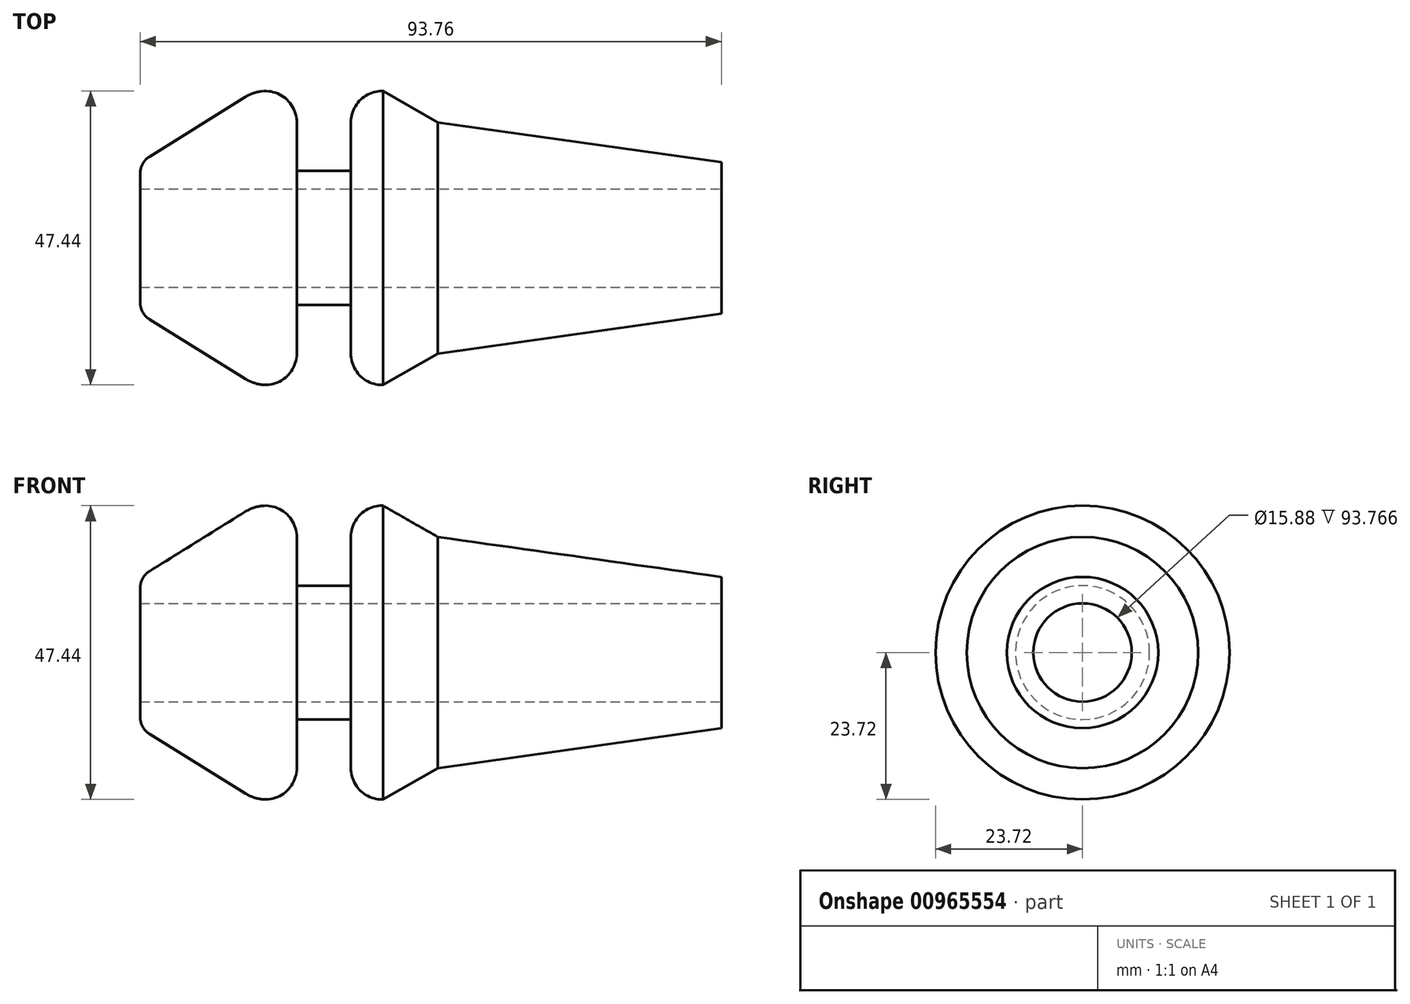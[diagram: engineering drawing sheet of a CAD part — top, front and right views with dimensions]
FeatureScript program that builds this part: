
annotation { "Feature Type Name" : "Feature", "Feature Type Description" : "" }
export const myFeature = defineFeature(function(context is Context, id is Id, definition is map)
    precondition{}
    {
        {
            var Q0;
            Q0=qCreatedBy(makeId("Top.planeOp"),FACE);
            var sketch = newSketch(context, id + "F0", { "sketchPlane" : qUnion([Q0])});
            skLineSegment(sketch, "E0", {"start": v(-39.16, 0) * mm, "end": v(-39.16, 12.21) * mm});
            skLineSegment(sketch, "E1", {"start": v(-39.16, 12.21) * mm, "end": v(-20.63, 23.72) * mm});
            skLineSegment(sketch, "E2", {"start": v(-20.63, 23.72) * mm, "end": v(-13.9, 23.72) * mm});
            skLineSegment(sketch, "E3", {"start": v(0, 23.72) * mm, "end": v(8.84, 18.67) * mm});
            skLineSegment(sketch, "E4", {"start": v(8.84, 18.67) * mm, "end": v(54.6, 12.21) * mm});
            skLineSegment(sketch, "E5", {"start": v(54.6, 12.21) * mm, "end": v(54.6, 0) * mm});
            skLineSegment(sketch, "E6", {"start": v(-39.16, 0) * mm, "end": v(54.6, 0) * mm});
            skLineSegment(sketch, "E7", {"start": v(-13.9, 23.72) * mm, "end": v(-13.9, 10.8) * mm});
            skLineSegment(sketch, "E8", {"start": v(-13.9, 10.8) * mm, "end": v(-5.2, 10.8) * mm});
            skLineSegment(sketch, "E9", {"start": v(-5.2, 10.8) * mm, "end": v(-5.2, 23.72) * mm});
            skLineSegment(sketch, "E10.trimOffspring", {"start": v(-5.2, 23.72) * mm, "end": v(0, 23.72) * mm});
            skSolve(sketch);
        }
        {
            var Q0;
            Q0=makeQuery(id+"F0.imprint","IMPRINT",FACE,{"disambiguationData":[TD([[makeQuery(id+"F0.imprint","IMPRINT",EDGE,{"derivedFrom":sQuery(id+"F0.wireOp",EDGE,"E0")}),-1.0]])]});
            var Q1;
            Q1=sQuery(id+"F0.wireOp",EDGE,"E6");
            revolve(context, id + "F1", {"surfaceOperationType" : NewSurfaceOperationType.NEW, "entities" : qUnion([Q0]), "axis" : qUnion([Q1]), "revolveType" : RevolveType.FULL});
        }
        {
            var Q0;
            Q0=makeQuery(id+"F1.opRevolve","SWEPT_EDGE",EDGE,{"disambiguationData":[OSD([sQuery(id+"F0.wireOp",EDGE,"E1"),sQuery(id+"F0.wireOp",EDGE,"E2")])]});
            fillet(context, id + "F2", {"entities" : qUnion([Q0]), "radius" : 6.35 * mm, "tangentPropagation" : true, "allowEdgeOverflow" : false});
        }
        {
            var Q0;
            Q0=makeQuery(id+"F1.opRevolve","SWEPT_FACE",FACE,{"disambiguationData":[OSD([sQuery(id+"F0.wireOp",EDGE,"E5")])]});
            var sketch = newSketch(context, id + "F3", { "sketchPlane" : qUnion([Q0])});
            skCircle(sketch, "E11", {"center": v(0, 0) * mm, "radius": 7.94 * mm});
            skSolve(sketch);
        }
        {
            var Q0;
            Q0=makeQuery(id+"F3.imprint","IMPRINT",FACE,{"disambiguationData":[TD([[makeQuery(id+"F3.imprint","IMPRINT",EDGE,{"derivedFrom":sQuery(id+"F3.wireOp",EDGE,"E11")}),1.0]])]});
            var Q1;
            Q1=makeQuery(id+"F1.opRevolve","SWEPT_FACE",FACE,{"disambiguationData":[OSD([sQuery(id+"F0.wireOp",EDGE,"E1")])]});
            extrude(context, id + "F4", {"entities" : qUnion([Q0]), "operationType" : NewBodyOperationType.REMOVE, "endBound" : BoundingType.UP_TO_NEXT, "oppositeDirection" : true, "depth" : 25.4 * mm, "endBoundEntityFace" : qUnion([Q1]), "offsetDistance" : 25.4 * mm});
        }
        {
            var Q0;
            Q0=makeQuery(id+"F1.opRevolve","SWEPT_EDGE",EDGE,{"disambiguationData":[OSD([sQuery(id+"F0.wireOp",EDGE,"E0"),sQuery(id+"F0.wireOp",EDGE,"E1")])]});
            fillet(context, id + "F5", {"entities" : qUnion([Q0]), "radius" : 3.17 * mm, "tangentPropagation" : true, "allowEdgeOverflow" : false});
        }
        {
            var Q0;
            Q0=makeQuery(id+"F1.opRevolve","SWEPT_EDGE",EDGE,{"disambiguationData":[OSD([sQuery(id+"F0.wireOp",EDGE,"E2"),sQuery(id+"F0.wireOp",EDGE,"E7")])]});
            var Q1;
            Q1=makeQuery(id+"F1.opRevolve","SWEPT_EDGE",EDGE,{"disambiguationData":[OSD([sQuery(id+"F0.wireOp",EDGE,"E9"),sQuery(id+"F0.wireOp",EDGE,"E10.trimOffspring")])]});
            fillet(context, id + "F6", {"entities" : qUnion([Q0, Q1]), "radius" : 5.08 * mm, "tangentPropagation" : true, "allowEdgeOverflow" : false});
        }
    });
